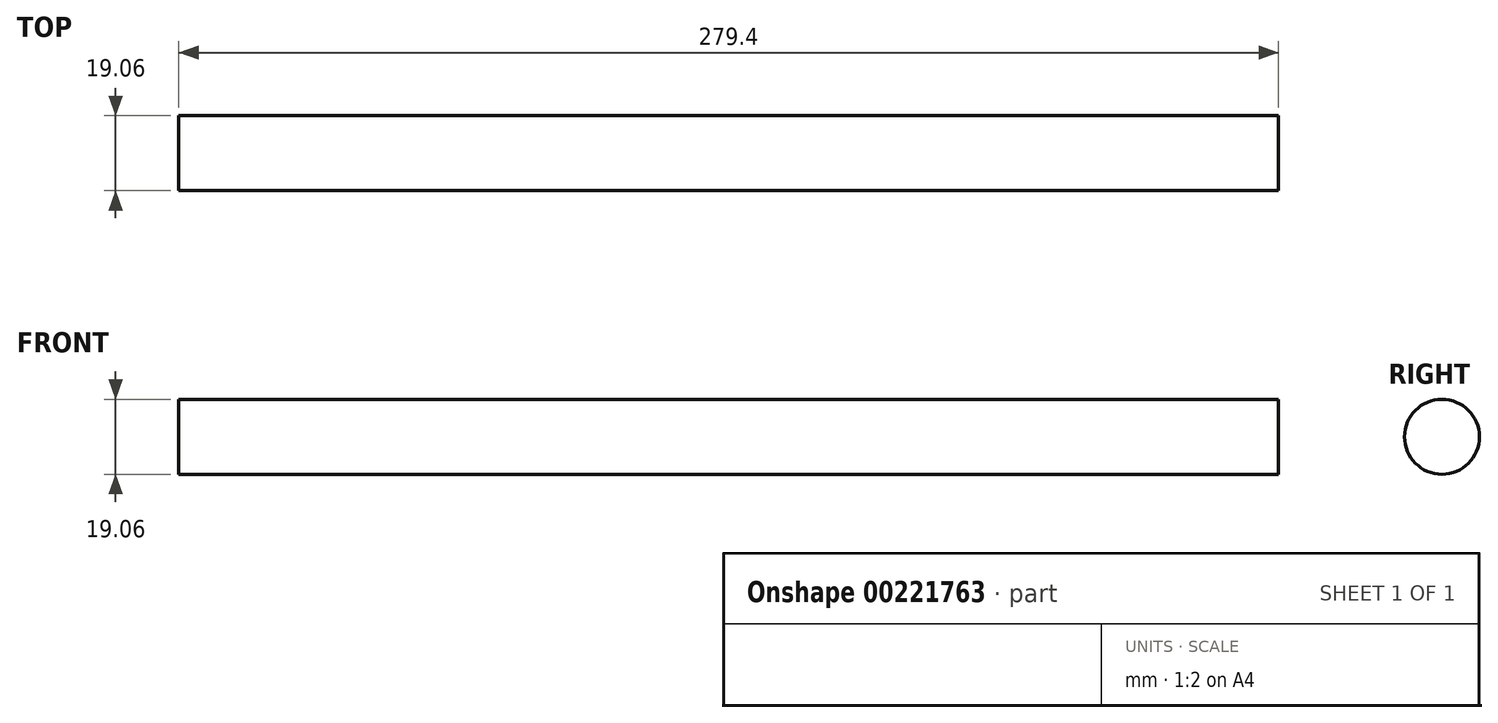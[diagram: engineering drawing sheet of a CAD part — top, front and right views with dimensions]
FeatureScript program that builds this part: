
annotation { "Feature Type Name" : "Feature", "Feature Type Description" : "" }
export const myFeature = defineFeature(function(context is Context, id is Id, definition is map)
    precondition{}
    {
        {
            var Q0;
            Q0=qCreatedBy(makeId("Right.planeOp"),FACE);
            var sketch = newSketch(context, id + "F0", { "sketchPlane" : qUnion([Q0])});
            skCircle(sketch, "E0", {"center": v(0, 0) * mm, "radius": 9.53 * mm});
            skSolve(sketch);
        }
        {
            var Q0;
            Q0 = qSketchRegion(id + "F0", true);
            extrude(context, id + "F1", {"entities" : qUnion([Q0]), "oppositeDirection" : true, "depth" : 279.4 * mm});
        }
    });
